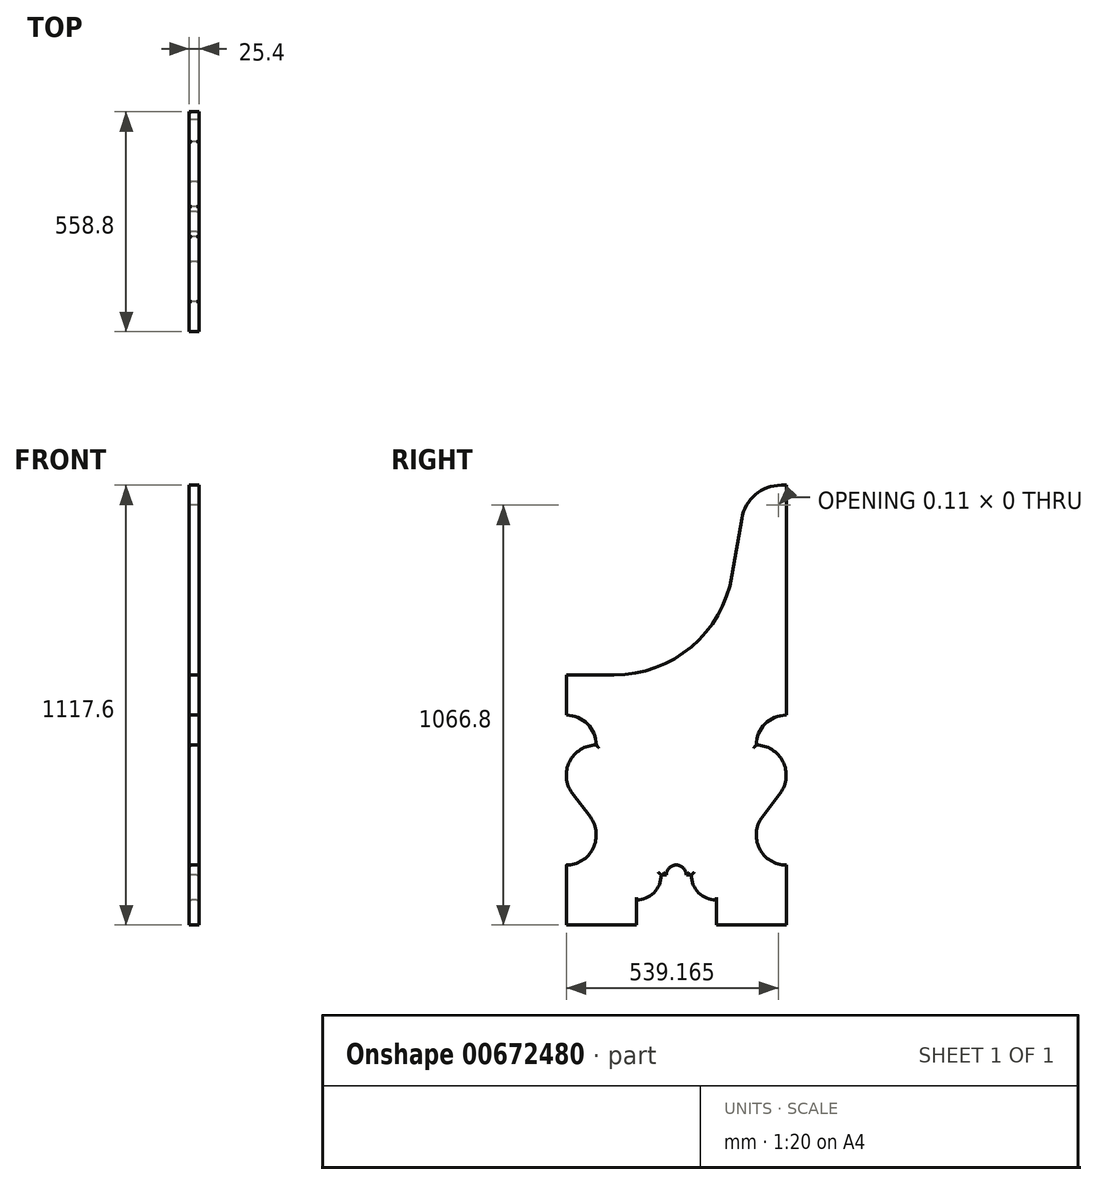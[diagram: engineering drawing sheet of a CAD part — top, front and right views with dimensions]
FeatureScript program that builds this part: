
annotation { "Feature Type Name" : "Feature", "Feature Type Description" : "" }
export const myFeature = defineFeature(function(context is Context, id is Id, definition is map)
    precondition{}
    {
        {
            var Q0;
            Q0=qCreatedBy(makeId("Right.planeOp"),FACE);
            var sketch = newSketch(context, id + "F0", { "sketchPlane" : qUnion([Q0])});
            skLineSegment(sketch, "E0.bottom", {"start": v(-279.4, 0) * mm, "end": v(-101.6, 0) * mm});
            skLineSegment(sketch, "E0.right", {"start": v(279.4, 0) * mm, "end": v(279.4, 152.4) * mm});
            skLineSegment(sketch, "E1.bottom", {"start": v(-279.4, 152.4) * mm, "end": v(-203.2, 152.4) * mm, "construction": true});
            skLineSegment(sketch, "E1.top", {"start": v(-241.3, 304.8) * mm, "end": v(-203.2, 304.8) * mm});
            skLineSegment(sketch, "E1.right", {"start": v(-203.2, 152.4) * mm, "end": v(-203.2, 304.8) * mm, "construction": true});
            skLineSegment(sketch, "E2.bottom", {"start": v(-203.2, 304.8) * mm, "end": v(-241.3, 304.8) * mm, "construction": true});
            skPoint(sketch, "E3.visualSharp", {"position": v(-203.2, 152.4) * mm});
            skArc(sketch, "E4", {"start": v(-279.4, 152.4) * mm, "mid": v(-211.24, 194.52) * mm, "end": v(-218.44, 274.32) * mm});
            skArc(sketch, "E5", {"start": v(-203.2, 457.2) * mm, "mid": v(-271.36, 415.08) * mm, "end": v(-264.16, 335.28) * mm});
            skLineSegment(sketch, "E6", {"start": v(-218.44, 274.32) * mm, "end": v(-264.16, 335.28) * mm});
            skArc(sketch, "E7", {"start": v(-203.2, 457.2) * mm, "mid": v(-225.52, 511.08) * mm, "end": v(-279.4, 533.4) * mm});
            skLineSegment(sketch, "E8.trimOffspring", {"start": v(-279.4, 533.4) * mm, "end": v(-279.4, 635) * mm});
            skPoint(sketch, "E9.orphan", {"position": v(-279.4, 304.8) * mm});
            skLineSegment(sketch, "E10", {"start": v(0, 0) * mm, "end": v(0, 1066.8) * mm, "construction": true});
            skLineSegment(sketch, "E11.left", {"start": v(-101.6, 0) * mm, "end": v(-101.6, 63.5) * mm});
            skLineSegment(sketch, "E11.right", {"start": v(101.6, 0) * mm, "end": v(101.6, 63.5) * mm});
            skArc(sketch, "E12", {"start": v(25.4, 127) * mm, "mid": v(17.96, 144.96) * mm, "end": v(0, 152.4) * mm});
            skLineSegment(sketch, "E13", {"start": v(25.4, 127) * mm, "end": v(38.1, 127) * mm});
            skArc(sketch, "E14", {"start": v(38.1, 127) * mm, "mid": v(56.7, 82.1) * mm, "end": v(101.6, 63.5) * mm});
            skArc(sketch, "E15.MirrorCS", {"start": v(-25.4, 127) * mm, "mid": v(-17.96, 144.96) * mm, "end": v(0, 152.4) * mm});
            skLineSegment(sketch, "E16.MirrorCS", {"start": v(-25.4, 127) * mm, "end": v(-38.1, 127) * mm});
            skArc(sketch, "E17.MirrorCS", {"start": v(-38.1, 127) * mm, "mid": v(-56.7, 82.1) * mm, "end": v(-101.6, 63.5) * mm});
            skLineSegment(sketch, "E18.trimOffspring", {"start": v(101.6, 0) * mm, "end": v(279.4, 0) * mm});
            skArc(sketch, "E19.MirrorCS", {"start": v(203.2, 457.2) * mm, "mid": v(225.52, 511.08) * mm, "end": v(279.4, 533.4) * mm});
            skArc(sketch, "E20.MirrorCS", {"start": v(203.2, 457.2) * mm, "mid": v(271.36, 415.08) * mm, "end": v(264.16, 335.28) * mm});
            skLineSegment(sketch, "E21.MirrorCS", {"start": v(218.44, 274.32) * mm, "end": v(264.16, 335.28) * mm});
            skArc(sketch, "E22.MirrorCS", {"start": v(279.4, 152.4) * mm, "mid": v(211.24, 194.52) * mm, "end": v(218.44, 274.32) * mm});
            skLineSegment(sketch, "E23.trimOffspring", {"start": v(279.4, 533.4) * mm, "end": v(279.4, 1117.6) * mm});
            skLineSegment(sketch, "E24", {"start": v(-279.4, 152.4) * mm, "end": v(-279.4, 0) * mm});
            skLineSegment(sketch, "E25", {"start": v(177.8, 406.4) * mm, "end": v(0, 406.4) * mm, "construction": true});
            skLineSegment(sketch, "E26.MirrorCS", {"start": v(-228.6, 406.4) * mm, "end": v(0, 406.4) * mm, "construction": true});
            skLineSegment(sketch, "E27", {"start": v(-279.4, 635) * mm, "end": v(-158.34, 635) * mm});
            skPoint(sketch, "E28.orphan", {"position": v(279.4, 1117.6) * mm});
            skLineSegment(sketch, "E29.trimOffspring", {"start": v(259.7, 1066.8) * mm, "end": v(259.82, 1066.8) * mm});
            skArc(sketch, "E30.trimOffspring", {"start": v(259.82, 1066.8) * mm, "mid": v(259.76, 1066.8) * mm, "end": v(259.7, 1066.8) * mm});
            skLineSegment(sketch, "E31", {"start": v(279.4, 1117.6) * mm, "end": v(266.7, 1117.6) * mm});
            skLineSegment(sketch, "E32", {"start": v(166.52, 1032.93) * mm, "end": v(142.2, 889) * mm});
            skPoint(sketch, "E33.visualSharp", {"position": v(99.26, 635) * mm});
            skArc(sketch, "E33.filletArc", {"start": v(-158.34, 635) * mm, "mid": v(38.4, 707) * mm, "end": v(142.2, 889) * mm});
            skPoint(sketch, "E34.visualSharp", {"position": v(180.83, 1117.6) * mm});
            skArc(sketch, "E34.filletArc", {"start": v(266.7, 1117.6) * mm, "mid": v(201.12, 1093.6) * mm, "end": v(166.52, 1032.93) * mm});
            skLineSegment(sketch, "E35", {"start": v(177.8, 406.4) * mm, "end": v(241.3, 1012.68) * mm, "construction": true});
            skSolve(sketch);
        }
        {
            var Q0;
            Q0=makeQuery(id+"F0.imprint","IMPRINT",FACE,{"disambiguationData":[TD([[makeQuery(id+"F0.imprint","IMPRINT",EDGE,{"derivedFrom":sQuery(id+"F0.wireOp",EDGE,"E0.bottom")}),1.0]])]});
            extrude(context, id + "F1", {"entities" : qUnion([Q0]), "depth" : 12.7 * mm, "offsetDistance" : 25.4 * mm, "hasSecondDirection" : true, "secondDirectionOppositeDirection" : true, "secondDirectionDepth" : 12.7 * mm});
        }
        {
            var Q0;
            Q0=makeQuery(id+"F1.opExtrude","CAP_EDGE",EDGE,{"disambiguationData":[OSD([sQuery(id+"F0.wireOp",EDGE,"E4")])],"isStart":false});
            var Q1;
            Q1=makeQuery(id+"F1.opExtrude","CAP_EDGE",EDGE,{"disambiguationData":[OSD([sQuery(id+"F0.wireOp",EDGE,"E7")])],"isStart":false});
            var Q2;
            Q2=makeQuery(id+"F1.opExtrude","CAP_EDGE",EDGE,{"disambiguationData":[OSD([sQuery(id+"F0.wireOp",EDGE,"E4")])],"isStart":true});
            var Q3;
            Q3=makeQuery(id+"F1.opExtrude","CAP_EDGE",EDGE,{"disambiguationData":[OSD([sQuery(id+"F0.wireOp",EDGE,"E7")])],"isStart":true});
            var Q4;
            Q4=makeQuery(id+"F1.opExtrude","CAP_EDGE",EDGE,{"disambiguationData":[OSD([sQuery(id+"F0.wireOp",EDGE,"E22.MirrorCS")])],"isStart":false});
            var Q5;
            Q5=makeQuery(id+"F1.opExtrude","CAP_EDGE",EDGE,{"disambiguationData":[OSD([sQuery(id+"F0.wireOp",EDGE,"E22.MirrorCS")])],"isStart":true});
            var Q6;
            Q6=makeQuery(id+"F1.opExtrude","CAP_EDGE",EDGE,{"disambiguationData":[OSD([sQuery(id+"F0.wireOp",EDGE,"E19.MirrorCS")])],"isStart":true});
            var Q7;
            Q7=makeQuery(id+"F1.opExtrude","CAP_EDGE",EDGE,{"disambiguationData":[OSD([sQuery(id+"F0.wireOp",EDGE,"E19.MirrorCS")])],"isStart":false});
            var Q8;
            Q8=makeQuery(id+"F1.opExtrude","CAP_EDGE",EDGE,{"disambiguationData":[OSD([sQuery(id+"F0.wireOp",EDGE,"E17.MirrorCS")])],"isStart":false});
            var Q9;
            Q9=makeQuery(id+"F1.opExtrude","CAP_EDGE",EDGE,{"disambiguationData":[OSD([sQuery(id+"F0.wireOp",EDGE,"E17.MirrorCS")])],"isStart":true});
            var Q10;
            Q10=makeQuery(id+"F1.opExtrude","CAP_EDGE",EDGE,{"disambiguationData":[OSD([sQuery(id+"F0.wireOp",EDGE,"E14")])],"isStart":false});
            var Q11;
            Q11=makeQuery(id+"F1.opExtrude","CAP_EDGE",EDGE,{"disambiguationData":[OSD([sQuery(id+"F0.wireOp",EDGE,"E14")])],"isStart":true});
            var Q12;
            Q12=makeQuery(id+"F1.opExtrude","CAP_EDGE",EDGE,{"disambiguationData":[OSD([sQuery(id+"F0.wireOp",EDGE,"E12"),sQuery(id+"F0.wireOp",EDGE,"E15.MirrorCS")])],"isStart":false});
            var Q13;
            Q13=makeQuery(id+"F1.opExtrude","CAP_EDGE",EDGE,{"disambiguationData":[OSD([sQuery(id+"F0.wireOp",EDGE,"E12"),sQuery(id+"F0.wireOp",EDGE,"E15.MirrorCS")])],"isStart":true});
            var Q14;
            Q14=makeQuery(id+"F1.opExtrude","CAP_EDGE",EDGE,{"disambiguationData":[OSD([sQuery(id+"F0.wireOp",EDGE,"E13")])],"isStart":true});
            var Q15;
            Q15=makeQuery(id+"F1.opExtrude","CAP_EDGE",EDGE,{"disambiguationData":[OSD([sQuery(id+"F0.wireOp",EDGE,"E13")])],"isStart":false});
            var Q16;
            Q16=makeQuery(id+"F1.opExtrude","CAP_EDGE",EDGE,{"disambiguationData":[OSD([sQuery(id+"F0.wireOp",EDGE,"E16.MirrorCS")])],"isStart":true});
            var Q17;
            Q17=makeQuery(id+"F1.opExtrude","CAP_EDGE",EDGE,{"disambiguationData":[OSD([sQuery(id+"F0.wireOp",EDGE,"E16.MirrorCS")])],"isStart":false});
            fillet(context, id + "F2", {"entities" : qUnion([Q0, Q1, Q2, Q3, Q4, Q5, Q6, Q7, Q8, Q9, Q10, Q11, Q12, Q13, Q14, Q15, Q16, Q17]), "radius" : 6.35 * mm, "tangentPropagation" : true, "allowEdgeOverflow" : false});
        }
    });
